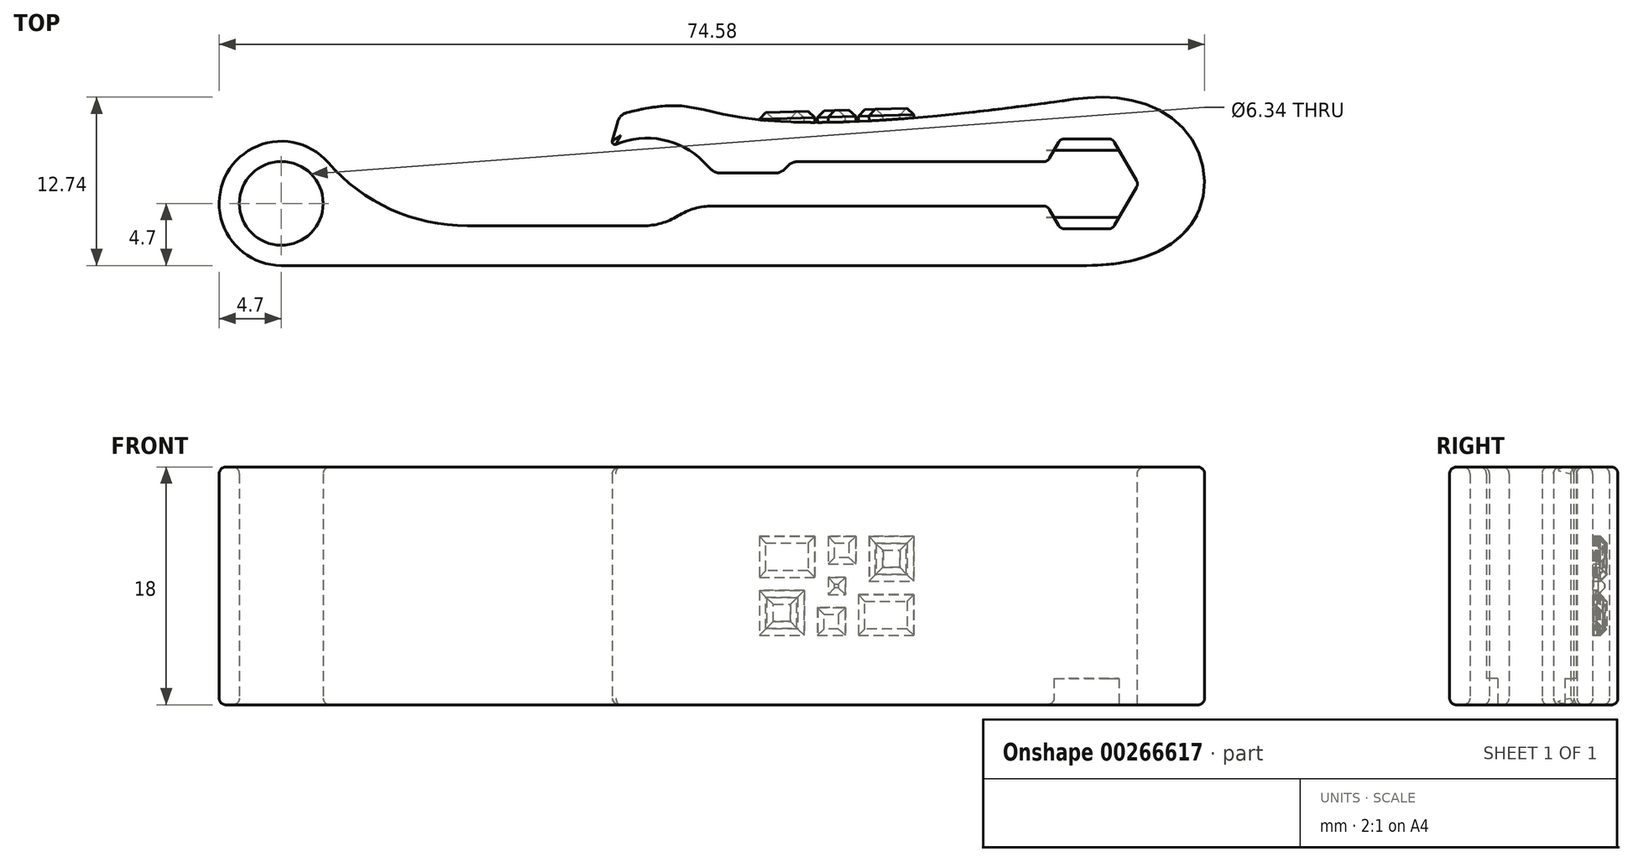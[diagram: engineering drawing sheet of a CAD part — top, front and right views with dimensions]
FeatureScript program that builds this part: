
annotation { "Feature Type Name" : "Feature", "Feature Type Description" : "" }
export const myFeature = defineFeature(function(context is Context, id is Id, definition is map)
    precondition{}
    {
        {
            var Q0;
            Q0=qCreatedBy(makeId("Top.planeOp"),FACE);
            var sketch = newSketch(context, id + "F0", { "sketchPlane" : qUnion([Q0])});
            skLineSegment(sketch, "E0", {"start": v(0, -4.7) * mm, "end": v(60.95, -4.7) * mm});
            skArc(sketch, "E1", {"start": v(0, -4.7) * mm, "mid": v(-4.28, 1.94) * mm, "end": v(3.54, 3.1) * mm});
            skArc(sketch, "E2.cCircle", {"start": v(57.4, -0.2) * mm, "mid": v(64.88, 1.48) * mm, "end": v(57.4, 3.16) * mm, "construction": true});
            skLineSegment(sketch, "E2.0", {"start": v(64.88, 1.48) * mm, "end": v(62.91, -1.92) * mm});
            skLineSegment(sketch, "E2.1", {"start": v(62.91, -1.93) * mm, "end": v(58.99, -1.93) * mm});
            skLineSegment(sketch, "E2.2", {"start": v(58.99, -1.92) * mm, "end": v(58, -0.2) * mm});
            skLineSegment(sketch, "E2.3", {"start": v(58, 3.16) * mm, "end": v(58.99, 4.88) * mm});
            skLineSegment(sketch, "E2.4", {"start": v(58.99, 4.88) * mm, "end": v(62.91, 4.88) * mm});
            skLineSegment(sketch, "E2.5", {"start": v(62.91, 4.88) * mm, "end": v(64.88, 1.48) * mm});
            skLineSegment(sketch, "E3", {"start": v(30.95, -0.2) * mm, "end": v(58, -0.2) * mm});
            skCircle(sketch, "E4", {"center": v(0, 0) * mm, "radius": 3.17 * mm});
            skLineSegment(sketch, "E5", {"start": v(58, 3.16) * mm, "end": v(38.67, 3.16) * mm});
            skLineSegment(sketch, "E6", {"start": v(38.67, 3.16) * mm, "end": v(37.81, 2.3) * mm});
            skLineSegment(sketch, "E7", {"start": v(37.81, 2.3) * mm, "end": v(32.81, 2.3) * mm});
            skPoint(sketch, "E8.orphan", {"position": v(57.02, 1.48) * mm});
            skLineSegment(sketch, "E9", {"start": v(32.81, 2.3) * mm, "end": v(31.95, 3.16) * mm});
            skLineSegment(sketch, "E10", {"start": v(24.95, 4.3) * mm, "end": v(25.6, 6.71) * mm});
            skFitSpline(sketch, "E11", {"points": [v(25.6, 6.71) * mm, v(59.95, 7.88) * mm], "startDerivative": vector(28.2, 7.76) * mm, "endDerivative": vector(95.5, 13.53) * mm});
            skArc(sketch, "E12", {"start": v(3.54, 3.1) * mm, "mid": v(8.3, -0.45) * mm, "end": v(14.09, -1.7) * mm});
            skLineSegment(sketch, "E13", {"start": v(14.09, -1.7) * mm, "end": v(27.38, -1.7) * mm});
            skArc(sketch, "E14", {"start": v(27.38, -1.7) * mm, "mid": v(29.32, -1.31) * mm, "end": v(30.95, -0.2) * mm});
            skArc(sketch, "E15", {"start": v(31.95, 3.16) * mm, "mid": v(28.63, 4.86) * mm, "end": v(24.95, 4.3) * mm});
            skFitSpline(sketch, "E16", {"points": [v(59.95, 7.88) * mm, v(69.88, 1.48) * mm, v(60.95, -4.7) * mm], "startDerivative": vector(41.13, 5.83) * mm, "endDerivative": vector(-36.78, 0) * mm});
            skLineSegment(sketch, "E17", {"start": v(59.95, 7.88) * mm, "end": v(70.38, 9.36) * mm, "construction": true});
            skLineSegment(sketch, "E18", {"start": v(64.88, 1.48) * mm, "end": v(75.73, 1.48) * mm, "construction": true});
            skLineSegment(sketch, "E19", {"start": v(60.95, -4.7) * mm, "end": v(60.95, 1.48) * mm, "construction": true});
            skLineSegment(sketch, "E20", {"start": v(58.49, 4.02) * mm, "end": v(63.41, 4.02) * mm});
            skLineSegment(sketch, "E21", {"start": v(58.49, -1.06) * mm, "end": v(63.41, -1.06) * mm});
            skLineSegment(sketch, "E22", {"start": v(-5.74, -3.5) * mm, "end": v(-8.78, -3.77) * mm});
            skLineSegment(sketch, "E23", {"start": v(0, -4.7) * mm, "end": v(-8, -4.7) * mm});
            skArc(sketch, "E24", {"start": v(-5.74, -3.5) * mm, "mid": v(-4.6, -2.83) * mm, "end": v(-4.45, -1.52) * mm});
            skLineSegment(sketch, "E25", {"start": v(-8, -4.7) * mm, "end": v(-8.78, -3.77) * mm});
            skLineSegment(sketch, "E26", {"start": v(-8, -4.7) * mm, "end": v(-8, -3.7) * mm, "construction": true});
            skLineSegment(sketch, "E27", {"start": v(38.67, 3.16) * mm, "end": v(38.67, 6.16) * mm, "construction": true});
            skSolve(sketch);
        }
        {
            var Q0;
            Q0=makeQuery(id+"F0.imprint","IMPRINT",FACE,{"disambiguationData":[TD([[makeQuery(id+"F0.imprint","IMPRINT",EDGE,{"derivedFrom":sQuery(id+"F0.wireOp",EDGE,"E0")}),1.0]])]});
            extrude(context, id + "F1", {"entities" : qUnion([Q0]), "depth" : 18 * mm});
        }
        {
            var Q0;
            {var subQ0=sQuery(id+"F0.wireOp",EDGE,"E2.1");Q0=makeQuery(id+"F0.imprint","IMPRINT",FACE,{"disambiguationData":[TD([[makeQuery(id+"F0.imprint","IMPRINT",EDGE,{"derivedFrom":subQ0}),-1.0]])]});}
            var Q1;
            {var subQ0=sQuery(id+"F0.wireOp",EDGE,"E2.4");Q1=makeQuery(id+"F0.imprint","IMPRINT",FACE,{"disambiguationData":[TD([[makeQuery(id+"F0.imprint","IMPRINT",EDGE,{"derivedFrom":subQ0}),-1.0]])]});}
            extrude(context, id + "F2", {"entities" : qUnion([Q0, Q1]), "operationType" : NewBodyOperationType.ADD, "depth" : 2 * mm});
        }
        {
            var Q0;
            Q0=makeQuery(id+"F1.opExtrude","SWEPT_EDGE",EDGE,{"disambiguationData":[OSD([sQuery(id+"F0.wireOp",EDGE,"E10"),sQuery(id+"F0.wireOp",EDGE,"E15")])]});
            var Q1;
            Q1=makeQuery(id+"F1.opExtrude","SWEPT_EDGE",EDGE,{"disambiguationData":[OSD([sQuery(id+"F0.wireOp",EDGE,"E22"),sQuery(id+"F0.wireOp",EDGE,"E25")])]});
            var Q2;
            Q2=makeQuery(id+"F1.opExtrude","SWEPT_EDGE",EDGE,{"disambiguationData":[OSD([sQuery(id+"F0.wireOp",EDGE,"E23"),sQuery(id+"F0.wireOp",EDGE,"E25")])]});
            fillet(context, id + "F3", {"entities" : qUnion([Q0, Q1, Q2]), "radius" : 0.2 * mm, "tangentPropagation" : true, "allowEdgeOverflow" : false});
        }
        {
            var Q0;
            Q0=makeQuery(id+"F1.opExtrude","SWEPT_EDGE",EDGE,{"disambiguationData":[OSD([sQuery(id+"F0.wireOp",EDGE,"E10"),sQuery(id+"F0.wireOp",EDGE,"E11")])]});
            fillet(context, id + "F4", {"entities" : qUnion([Q0]), "radius" : 1 * mm, "tangentPropagation" : true, "allowEdgeOverflow" : false});
        }
        {
            var Q0;
            Q0=makeQuery(id+"F1.opExtrude","SWEPT_EDGE",EDGE,{"disambiguationData":[OSD([sQuery(id+"F0.wireOp",EDGE,"E7"),sQuery(id+"F0.wireOp",EDGE,"E9")])]});
            var Q1;
            Q1=makeQuery(id+"F1.opExtrude","SWEPT_EDGE",EDGE,{"disambiguationData":[OSD([sQuery(id+"F0.wireOp",EDGE,"E5"),sQuery(id+"F0.wireOp",EDGE,"E6")])]});
            var Q2;
            Q2=makeQuery(id+"F1.opExtrude","SWEPT_EDGE",EDGE,{"disambiguationData":[OSD([sQuery(id+"F0.wireOp",EDGE,"E6"),sQuery(id+"F0.wireOp",EDGE,"E7")])]});
            fillet(context, id + "F5", {"entities" : qUnion([Q0, Q1, Q2]), "radius" : 1 * mm, "tangentPropagation" : true, "allowEdgeOverflow" : false});
        }
        {
            var Q0;
            Q0=makeQuery(id+"F1.opExtrude","SWEPT_EDGE",EDGE,{"disambiguationData":[OSD([sQuery(id+"F0.wireOp",EDGE,"E3"),sQuery(id+"F0.wireOp",EDGE,"E14")])]});
            fillet(context, id + "F6", {"entities" : qUnion([Q0]), "radius" : 5 * mm, "tangentPropagation" : true, "allowEdgeOverflow" : false});
        }
        {
            var Q0;
            Q0=makeQuery(id+"F1.opExtrude","SWEPT_EDGE",EDGE,{"disambiguationData":[OSD([sQuery(id+"F0.wireOp",EDGE,"E2.0"),sQuery(id+"F0.wireOp",EDGE,"E2.5")])]});
            var Q1;
            Q1=makeQuery(id+"F1.opExtrude","SWEPT_EDGE",EDGE,{"disambiguationData":[OSD([sQuery(id+"F0.wireOp",EDGE,"E2.0"),sQuery(id+"F0.wireOp",EDGE,"E2.1")])]});
            var Q2;
            Q2=makeQuery(id+"F1.opExtrude","SWEPT_EDGE",EDGE,{"disambiguationData":[OSD([sQuery(id+"F0.wireOp",EDGE,"E2.4"),sQuery(id+"F0.wireOp",EDGE,"E2.5")])]});
            var Q3;
            Q3=makeQuery(id+"F1.opExtrude","SWEPT_EDGE",EDGE,{"disambiguationData":[OSD([sQuery(id+"F0.wireOp",EDGE,"E2.3"),sQuery(id+"F0.wireOp",EDGE,"E2.4")])]});
            var Q4;
            Q4=makeQuery(id+"F1.opExtrude","SWEPT_EDGE",EDGE,{"disambiguationData":[OSD([sQuery(id+"F0.wireOp",EDGE,"E2.3"),sQuery(id+"F0.wireOp",EDGE,"E5")])]});
            var Q5;
            Q5=makeQuery(id+"F1.opExtrude","SWEPT_EDGE",EDGE,{"disambiguationData":[OSD([sQuery(id+"F0.wireOp",EDGE,"E2.2"),sQuery(id+"F0.wireOp",EDGE,"E3")])]});
            var Q6;
            Q6=makeQuery(id+"F1.opExtrude","SWEPT_EDGE",EDGE,{"disambiguationData":[OSD([sQuery(id+"F0.wireOp",EDGE,"E2.1"),sQuery(id+"F0.wireOp",EDGE,"E2.2")])]});
            var Q7;
            Q7=makeQuery(id+"F2.opExtrude","SWEPT_EDGE",EDGE,{"disambiguationData":[OSD([sQuery(id+"F0.wireOp",EDGE,"E2.2"),sQuery(id+"F0.wireOp",EDGE,"E21")])]});
            var Q8;
            Q8=makeQuery(id+"F2.opExtrude","SWEPT_EDGE",EDGE,{"disambiguationData":[OSD([sQuery(id+"F0.wireOp",EDGE,"E2.0"),sQuery(id+"F0.wireOp",EDGE,"E21")])]});
            var Q9;
            Q9=makeQuery(id+"F2.opExtrude","SWEPT_EDGE",EDGE,{"disambiguationData":[OSD([sQuery(id+"F0.wireOp",EDGE,"E2.5"),sQuery(id+"F0.wireOp",EDGE,"E20")])]});
            var Q10;
            Q10=makeQuery(id+"F2.opExtrude","SWEPT_EDGE",EDGE,{"disambiguationData":[OSD([sQuery(id+"F0.wireOp",EDGE,"E2.3"),sQuery(id+"F0.wireOp",EDGE,"E20")])]});
            fillet(context, id + "F7", {"entities" : qUnion([Q0, Q1, Q2, Q3, Q4, Q5, Q6, Q7, Q8, Q9, Q10]), "radius" : 0.5 * mm, "tangentPropagation" : true, "allowEdgeOverflow" : false});
        }
        {
            var Q0;
            Q0=makeQuery(id+"F1.opExtrude","CAP_EDGE",EDGE,{"disambiguationData":[OSD([sQuery(id+"F0.wireOp",EDGE,"E11")])],"isStart":true});
            var Q1;
            Q1=makeQuery(id+"F1.opExtrude","CAP_EDGE",EDGE,{"disambiguationData":[OSD([sQuery(id+"F0.wireOp",EDGE,"afd7a44a-d7ef-45fa-91de-e0b89ce8b458")])],"isStart":false});
            var Q2;
            Q2=makeQuery(id+"F1.opExtrude","CAP_EDGE",EDGE,{"disambiguationData":[OSD([sQuery(id+"F0.wireOp",EDGE,"E4")])],"isStart":true});
            var Q3;
            Q3=makeQuery(id+"F1.opExtrude","CAP_EDGE",EDGE,{"disambiguationData":[OSD([sQuery(id+"F0.wireOp",EDGE,"E4")])],"isStart":false});
            var Q4;
            Q4=makeQuery(id+"F1.opExtrude","CAP_FACE",FACE,{"disambiguationData":[OSD([sQuery(id+"F0.wireOp",EDGE,"E0"),sQuery(id+"F0.wireOp",EDGE,"E1"),sQuery(id+"F0.wireOp",EDGE,"E2.0"),sQuery(id+"F0.wireOp",EDGE,"E2.1"),sQuery(id+"F0.wireOp",EDGE,"E2.2"),sQuery(id+"F0.wireOp",EDGE,"E2.3"),sQuery(id+"F0.wireOp",EDGE,"E2.4"),sQuery(id+"F0.wireOp",EDGE,"E2.5"),sQuery(id+"F0.wireOp",EDGE,"E3"),sQuery(id+"F0.wireOp",EDGE,"E4"),sQuery(id+"F0.wireOp",EDGE,"E5"),sQuery(id+"F0.wireOp",EDGE,"E6"),sQuery(id+"F0.wireOp",EDGE,"E7"),sQuery(id+"F0.wireOp",EDGE,"E9"),sQuery(id+"F0.wireOp",EDGE,"E10"),sQuery(id+"F0.wireOp",EDGE,"E11"),sQuery(id+"F0.wireOp",EDGE,"E12"),sQuery(id+"F0.wireOp",EDGE,"E13"),sQuery(id+"F0.wireOp",EDGE,"E14"),sQuery(id+"F0.wireOp",EDGE,"E15"),sQuery(id+"F0.wireOp",EDGE,"E16")])],"isStart":false});
            fillet(context, id + "F8", {"entities" : qUnion([Q0, Q1, Q2, Q3, Q4]), "radius" : 0.5 * mm, "tangentPropagation" : true, "allowEdgeOverflow" : false});
        }
        {
            var Q0;
            {var subQ0=sQuery(id+"F0.wireOp",EDGE,"E11");Q0=makeQuery(id+"F4.opFillet","BLEND_EDGE",EDGE,{"blendedFrom":[makeQuery(id+"F1.opExtrude","SWEPT_EDGE",EDGE,{"disambiguationData":[OSD([sQuery(id+"F0.wireOp",EDGE,"E10"),subQ0])]}),makeQuery(id+"F1.opExtrude","SWEPT_FACE",FACE,{"disambiguationData":[OSD([subQ0])]})],"blendedInto":[makeQuery(id+"F1.opExtrude","SWEPT_FACE",FACE,{"disambiguationData":[OSD([subQ0])]})]});}
            cPoint(context, id + "F9", {"entities" : qUnion([Q0]), "parameter" : 0.5});
        }
        {
            var Q0;
            Q0=makeQuery(id+"F1.opExtrude","SWEPT_EDGE",EDGE,{"disambiguationData":[OSD([sQuery(id+"F0.wireOp",EDGE,"afd7a44a-d7ef-45fa-91de-e0b89ce8b458"),sQuery(id+"F0.wireOp",EDGE,"E11")])]});
            var Q1;
            Q1=qCreatedBy(id+"F9",VERTEX);
            cPlane(context, id + "F10", {"entities" : qUnion([Q0, Q1]), "cplaneType" : CPlaneType.LINE_ANGLE, "offset" : 25 * mm, "angle" : 0 * degree, "width" : 150 * mm, "height" : 150 * mm});
        }
        {
            var Q0;
            Q0=qCreatedBy(id+"F10.planeOp",FACE);
            var sketch = newSketch(context, id + "F11", { "sketchPlane" : qUnion([Q0])});
            skLineSegment(sketch, "E28.bottom", {"start": v(-48.06, 12.75) * mm, "end": v(-44.66, 12.75) * mm});
            skLineSegment(sketch, "E28.top", {"start": v(-48.06, 9.35) * mm, "end": v(-44.66, 9.35) * mm});
            skLineSegment(sketch, "E28.left", {"start": v(-48.06, 12.75) * mm, "end": v(-48.06, 9.35) * mm});
            skLineSegment(sketch, "E28.right", {"start": v(-44.66, 12.75) * mm, "end": v(-44.66, 9.35) * mm});
            skLineSegment(sketch, "E29.bottom", {"start": v(-43.66, 12.75) * mm, "end": v(-41.56, 12.75) * mm});
            skLineSegment(sketch, "E29.top", {"start": v(-43.66, 10.65) * mm, "end": v(-41.56, 10.65) * mm});
            skLineSegment(sketch, "E29.left", {"start": v(-43.66, 12.75) * mm, "end": v(-43.66, 10.65) * mm});
            skLineSegment(sketch, "E29.right", {"start": v(-41.56, 12.75) * mm, "end": v(-41.56, 10.65) * mm});
            skLineSegment(sketch, "E30.bottom", {"start": v(-41.56, 9.65) * mm, "end": v(-42.86, 9.65) * mm});
            skLineSegment(sketch, "E30.top", {"start": v(-41.56, 8.35) * mm, "end": v(-42.86, 8.35) * mm});
            skLineSegment(sketch, "E30.left", {"start": v(-41.56, 9.65) * mm, "end": v(-41.56, 8.35) * mm});
            skLineSegment(sketch, "E30.right", {"start": v(-42.86, 9.65) * mm, "end": v(-42.86, 8.35) * mm});
            skLineSegment(sketch, "E31.bottom", {"start": v(-42.86, 7.35) * mm, "end": v(-40.76, 7.35) * mm});
            skLineSegment(sketch, "E31.top", {"start": v(-42.86, 5.25) * mm, "end": v(-40.76, 5.25) * mm});
            skLineSegment(sketch, "E31.left", {"start": v(-42.86, 7.35) * mm, "end": v(-42.86, 5.25) * mm});
            skLineSegment(sketch, "E31.right", {"start": v(-40.76, 7.35) * mm, "end": v(-40.76, 5.25) * mm});
            skLineSegment(sketch, "E32.bottom", {"start": v(-39.76, 8.65) * mm, "end": v(-36.36, 8.65) * mm});
            skLineSegment(sketch, "E32.top", {"start": v(-39.76, 5.25) * mm, "end": v(-36.36, 5.25) * mm});
            skLineSegment(sketch, "E32.left", {"start": v(-39.76, 8.65) * mm, "end": v(-39.76, 5.25) * mm});
            skLineSegment(sketch, "E32.right", {"start": v(-36.36, 8.65) * mm, "end": v(-36.36, 5.25) * mm});
            skLineSegment(sketch, "E33.bottom", {"start": v(-48.06, 8.35) * mm, "end": v(-43.86, 8.35) * mm});
            skLineSegment(sketch, "E33.top", {"start": v(-48.06, 5.25) * mm, "end": v(-43.86, 5.25) * mm});
            skLineSegment(sketch, "E33.left", {"start": v(-48.06, 8.35) * mm, "end": v(-48.06, 5.25) * mm});
            skLineSegment(sketch, "E33.right", {"start": v(-43.86, 8.35) * mm, "end": v(-43.86, 5.25) * mm});
            skLineSegment(sketch, "E34.bottom", {"start": v(-40.56, 12.75) * mm, "end": v(-36.36, 12.75) * mm});
            skLineSegment(sketch, "E34.top", {"start": v(-40.56, 9.65) * mm, "end": v(-36.36, 9.65) * mm});
            skLineSegment(sketch, "E34.left", {"start": v(-40.56, 12.75) * mm, "end": v(-40.56, 9.65) * mm});
            skLineSegment(sketch, "E34.right", {"start": v(-36.36, 12.75) * mm, "end": v(-36.36, 9.65) * mm});
            skLineSegment(sketch, "E35.bottom", {"start": v(-45.7, 11.7) * mm, "end": v(-47, 11.7) * mm});
            skLineSegment(sketch, "E35.top", {"start": v(-45.7, 10.4) * mm, "end": v(-47, 10.4) * mm});
            skLineSegment(sketch, "E35.left", {"start": v(-45.7, 11.7) * mm, "end": v(-45.7, 10.4) * mm});
            skLineSegment(sketch, "E35.right", {"start": v(-47, 11.7) * mm, "end": v(-47, 10.4) * mm});
            skLineSegment(sketch, "E36.bottom", {"start": v(-37.4, 7.6) * mm, "end": v(-38.7, 7.6) * mm});
            skLineSegment(sketch, "E36.top", {"start": v(-37.4, 6.3) * mm, "end": v(-38.7, 6.3) * mm});
            skLineSegment(sketch, "E36.left", {"start": v(-37.4, 7.6) * mm, "end": v(-37.4, 6.3) * mm});
            skLineSegment(sketch, "E36.right", {"start": v(-38.7, 7.6) * mm, "end": v(-38.7, 6.3) * mm});
            skPoint(sketch, "E37", {"position": v(-48.06, 11.05) * mm});
            skPoint(sketch, "E38", {"position": v(-46.36, 12.75) * mm});
            skPoint(sketch, "E39", {"position": v(-47, 11.05) * mm});
            skPoint(sketch, "E40", {"position": v(-46.36, 11.7) * mm});
            skPoint(sketch, "E41", {"position": v(-38.06, 8.65) * mm});
            skPoint(sketch, "E42", {"position": v(-39.76, 6.95) * mm});
            skPoint(sketch, "E43", {"position": v(-38.7, 6.95) * mm});
            skPoint(sketch, "E44", {"position": v(-38.06, 7.6) * mm});
            skLineSegment(sketch, "E45", {"start": v(-26.36, 9) * mm, "end": v(-33.36, 9) * mm, "construction": true});
            skLineSegment(sketch, "E46", {"start": v(-33.36, 9) * mm, "end": v(-33.36, 5.25) * mm, "construction": true});
            skSolve(sketch);
        }
        {
            var Q0;
            Q0=makeQuery(id+"F11.imprint","IMPRINT",FACE,{"disambiguationData":[TD([[makeQuery(id+"F11.imprint","IMPRINT",EDGE,{"derivedFrom":sQuery(id+"F11.wireOp",EDGE,"E28.bottom")}),-1.0]])]});
            var Q1;
            Q1=makeQuery(id+"F11.imprint","IMPRINT",FACE,{"disambiguationData":[TD([[makeQuery(id+"F11.imprint","IMPRINT",EDGE,{"derivedFrom":sQuery(id+"F11.wireOp",EDGE,"E29.bottom")}),-1.0]])]});
            var Q2;
            Q2=makeQuery(id+"F11.imprint","IMPRINT",FACE,{"disambiguationData":[TD([[makeQuery(id+"F11.imprint","IMPRINT",EDGE,{"derivedFrom":sQuery(id+"F11.wireOp",EDGE,"E34.bottom")}),-1.0]])]});
            var Q3;
            Q3=makeQuery(id+"F11.imprint","IMPRINT",FACE,{"disambiguationData":[TD([[makeQuery(id+"F11.imprint","IMPRINT",EDGE,{"derivedFrom":sQuery(id+"F11.wireOp",EDGE,"E32.bottom")}),-1.0]])]});
            var Q4;
            Q4=makeQuery(id+"F11.imprint","IMPRINT",FACE,{"disambiguationData":[TD([[makeQuery(id+"F11.imprint","IMPRINT",EDGE,{"derivedFrom":sQuery(id+"F11.wireOp",EDGE,"E31.bottom")}),-1.0]])]});
            var Q5;
            Q5=makeQuery(id+"F11.imprint","IMPRINT",FACE,{"disambiguationData":[TD([[makeQuery(id+"F11.imprint","IMPRINT",EDGE,{"derivedFrom":sQuery(id+"F11.wireOp",EDGE,"E33.bottom")}),-1.0]])]});
            var Q6;
            Q6=makeQuery(id+"F11.imprint","IMPRINT",FACE,{"disambiguationData":[TD([[makeQuery(id+"F11.imprint","IMPRINT",EDGE,{"derivedFrom":sQuery(id+"F11.wireOp",EDGE,"E30.bottom")}),1.0]])]});
            var Q7;
            Q7=makeQuery(id+"F1.opExtrude","SWEPT_FACE",FACE,{"disambiguationData":[OSD([sQuery(id+"F0.wireOp",EDGE,"E11")])]});
            extrude(context, id + "F12", {"entities" : qUnion([Q0, Q1, Q2, Q3, Q4, Q5, Q6]), "operationType" : NewBodyOperationType.ADD, "endBound" : BoundingType.UP_TO_SURFACE, "oppositeDirection" : true, "endBoundEntityFace" : qUnion([Q7]), "depth" : 5 * mm, "hasSecondDirection" : true, "secondDirectionOppositeDirection" : true, "secondDirectionDepth" : 0.3 * mm});
        }
        {
            var Q0;
            Q0=makeQuery(id+"F12.opExtrude","CAP_FACE",FACE,{"disambiguationData":[OSD([sQuery(id+"F11.wireOp",EDGE,"E33.bottom"),sQuery(id+"F11.wireOp",EDGE,"E33.top"),sQuery(id+"F11.wireOp",EDGE,"E33.left"),sQuery(id+"F11.wireOp",EDGE,"E33.right")])],"isStart":true});
            var Q1;
            Q1=makeQuery(id+"F12.opExtrude","CAP_FACE",FACE,{"disambiguationData":[OSD([sQuery(id+"F11.wireOp",EDGE,"E34.bottom"),sQuery(id+"F11.wireOp",EDGE,"E34.top"),sQuery(id+"F11.wireOp",EDGE,"E34.left"),sQuery(id+"F11.wireOp",EDGE,"E34.right")])],"isStart":true});
            extrude(context, id + "F13", {"entities" : qUnion([Q0, Q1]), "operationType" : NewBodyOperationType.ADD, "endBound" : BoundingType.UP_TO_NEXT, "oppositeDirection" : true, "depth" : 1 * mm});
        }
        {
            var Q0;
            Q0=makeQuery(id+"F12.opExtrude","CAP_FACE",FACE,{"disambiguationData":[OSD([sQuery(id+"F11.wireOp",EDGE,"E31.bottom"),sQuery(id+"F11.wireOp",EDGE,"E31.top"),sQuery(id+"F11.wireOp",EDGE,"E31.left"),sQuery(id+"F11.wireOp",EDGE,"E31.right")])],"isStart":true});
            var Q1;
            Q1=makeQuery(id+"F12.opExtrude","CAP_FACE",FACE,{"disambiguationData":[OSD([sQuery(id+"F11.wireOp",EDGE,"E29.bottom"),sQuery(id+"F11.wireOp",EDGE,"E29.top"),sQuery(id+"F11.wireOp",EDGE,"E29.left"),sQuery(id+"F11.wireOp",EDGE,"E29.right")])],"isStart":true});
            var Q2;
            Q2=makeQuery(id+"F12.opExtrude","CAP_FACE",FACE,{"disambiguationData":[OSD([sQuery(id+"F11.wireOp",EDGE,"E34.bottom"),sQuery(id+"F11.wireOp",EDGE,"E34.top"),sQuery(id+"F11.wireOp",EDGE,"E34.left"),sQuery(id+"F11.wireOp",EDGE,"E34.right")])],"isStart":true});
            var Q3;
            Q3=makeQuery(id+"F12.opExtrude","CAP_FACE",FACE,{"disambiguationData":[OSD([sQuery(id+"F11.wireOp",EDGE,"E33.bottom"),sQuery(id+"F11.wireOp",EDGE,"E33.top"),sQuery(id+"F11.wireOp",EDGE,"E33.left"),sQuery(id+"F11.wireOp",EDGE,"E33.right")])],"isStart":true});
            var Q4;
            Q4=makeQuery(id+"F12.opExtrude","CAP_FACE",FACE,{"disambiguationData":[OSD([sQuery(id+"F11.wireOp",EDGE,"E30.bottom"),sQuery(id+"F11.wireOp",EDGE,"E30.top"),sQuery(id+"F11.wireOp",EDGE,"E30.left"),sQuery(id+"F11.wireOp",EDGE,"E30.right")])],"isStart":true});
            var Q5;
            Q5=makeQuery(id+"F12.opExtrude","CAP_FACE",FACE,{"disambiguationData":[OSD([sQuery(id+"F11.wireOp",EDGE,"E32.bottom"),sQuery(id+"F11.wireOp",EDGE,"E32.top"),sQuery(id+"F11.wireOp",EDGE,"E32.left"),sQuery(id+"F11.wireOp",EDGE,"E32.right"),sQuery(id+"F11.wireOp",EDGE,"E36.bottom"),sQuery(id+"F11.wireOp",EDGE,"E36.top"),sQuery(id+"F11.wireOp",EDGE,"E36.left"),sQuery(id+"F11.wireOp",EDGE,"E36.right")])],"isStart":true});
            var Q6;
            Q6=makeQuery(id+"F12.opExtrude","CAP_FACE",FACE,{"disambiguationData":[OSD([sQuery(id+"F11.wireOp",EDGE,"E28.bottom"),sQuery(id+"F11.wireOp",EDGE,"E28.top"),sQuery(id+"F11.wireOp",EDGE,"E28.left"),sQuery(id+"F11.wireOp",EDGE,"E28.right"),sQuery(id+"F11.wireOp",EDGE,"E35.bottom"),sQuery(id+"F11.wireOp",EDGE,"E35.top"),sQuery(id+"F11.wireOp",EDGE,"E35.left"),sQuery(id+"F11.wireOp",EDGE,"E35.right")])],"isStart":true});
            chamfer(context, id + "F14", {"entities" : qUnion([Q0, Q1, Q2, Q3, Q4, Q5, Q6]), "width" : .5 * mm, "tangentPropagation" : true});
        }
    });
